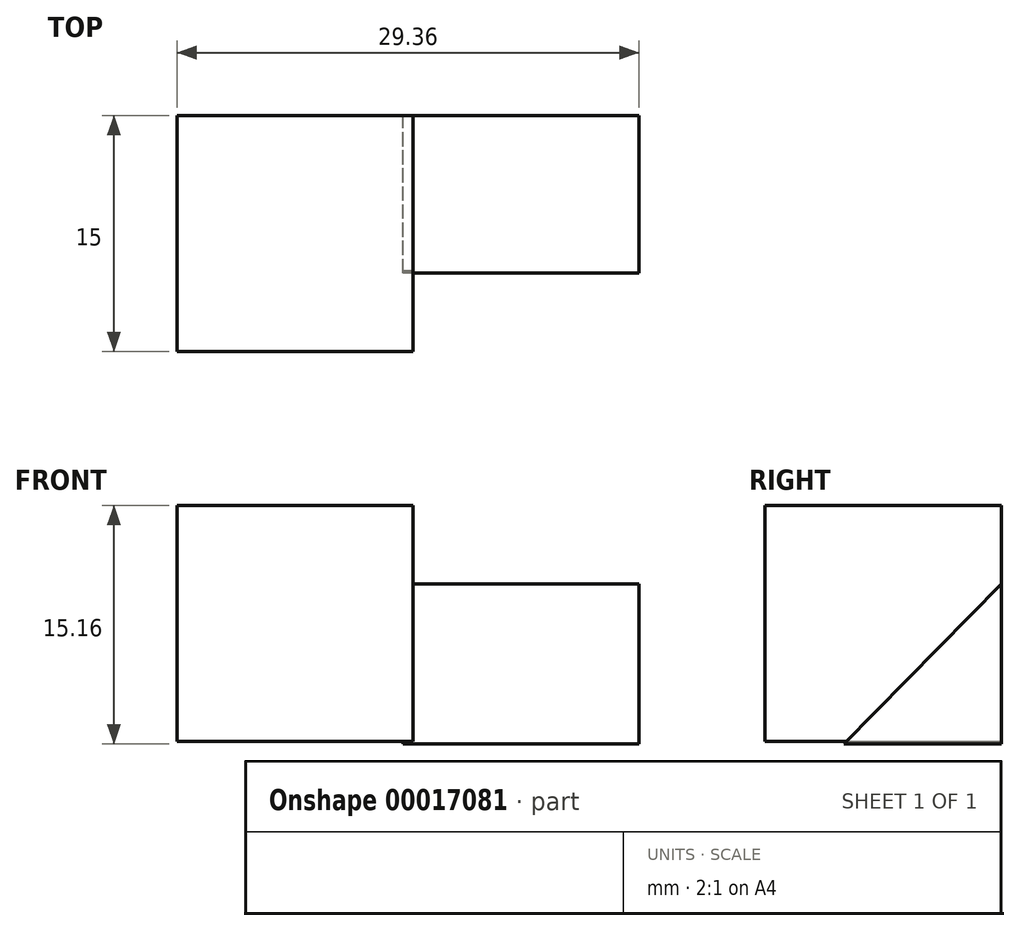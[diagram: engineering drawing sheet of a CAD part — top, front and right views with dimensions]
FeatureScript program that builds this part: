
annotation { "Feature Type Name" : "Feature", "Feature Type Description" : "" }
export const myFeature = defineFeature(function(context is Context, id is Id, definition is map)
    precondition{}
    {
        {
            var Q0;
            Q0=qCreatedBy(makeId("Front.planeOp"),FACE);
            var sketch = newSketch(context, id + "F0", { "sketchPlane" : qUnion([Q0])});
            skLineSegment(sketch, "E0.bottom", {"start": v(-14.36, 15.16) * mm, "end": v(0.64, 15.16) * mm});
            skLineSegment(sketch, "E0.top", {"start": v(-14.36, 0.16) * mm, "end": v(0.64, 0.16) * mm});
            skLineSegment(sketch, "E0.left", {"start": v(-14.36, 15.16) * mm, "end": v(-14.36, 0.16) * mm});
            skLineSegment(sketch, "E0.right", {"start": v(0.64, 15.16) * mm, "end": v(0.64, 0.16) * mm});
            skSolve(sketch);
        }
        {
            var Q0;
            Q0=makeQuery(id+"F0.imprint","IMPRINT",FACE,{"disambiguationData":[TD([[makeQuery(id+"F0.imprint","IMPRINT",EDGE,{"derivedFrom":sQuery(id+"F0.wireOp",EDGE,"E0.bottom")}),-1.0]])]});
            extrude(context, id + "F1", {"entities" : qUnion([Q0]), "depth" : 15 * mm});
        }
        {
            var Q0;
            Q0=qCreatedBy(makeId("Right.planeOp"),FACE);
            var sketch = newSketch(context, id + "F2", { "sketchPlane" : qUnion([Q0])});
            skLineSegment(sketch, "E1", {"start": v(-10, 0) * mm, "end": v(0, 10.16) * mm});
            skLineSegment(sketch, "E2", {"start": v(-10, 0) * mm, "end": v(0, 0) * mm});
            skLineSegment(sketch, "E3", {"start": v(0, 0) * mm, "end": v(0, 10.16) * mm});
            skSolve(sketch);
        }
        {
            var Q0;
            Q0 = qSketchRegion(id + "F2", true);
            extrude(context, id + "F3", {"entities" : qUnion([Q0]), "operationType" : NewBodyOperationType.ADD, "depth" : 15 * mm});
        }
    });
